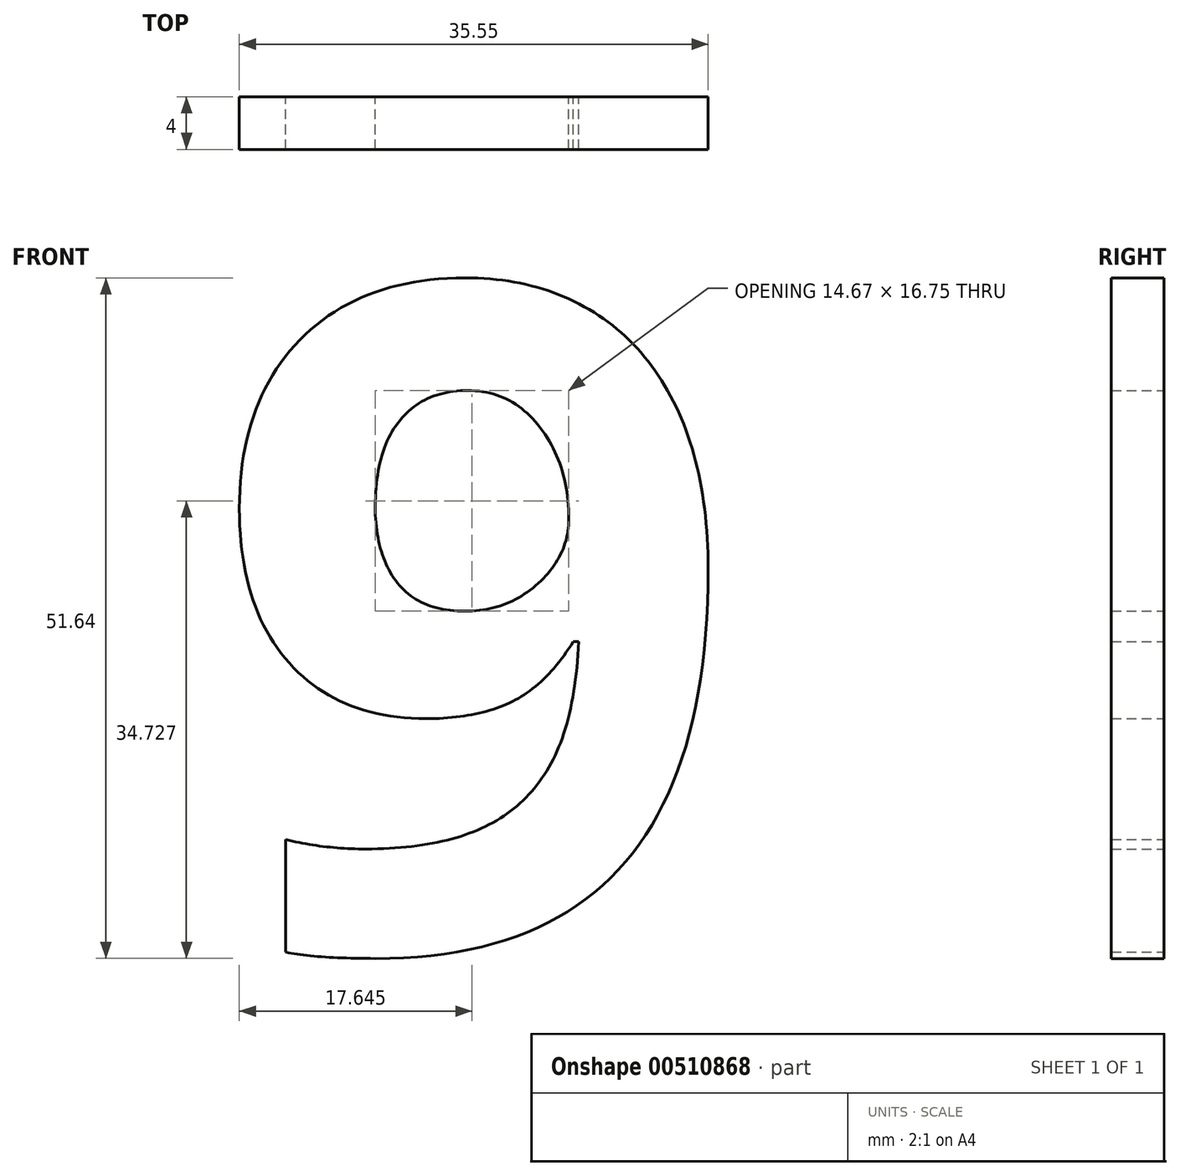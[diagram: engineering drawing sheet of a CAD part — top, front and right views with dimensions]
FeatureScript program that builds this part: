
annotation { "Feature Type Name" : "Feature", "Feature Type Description" : "" }
export const myFeature = defineFeature(function(context is Context, id is Id, definition is map)
    precondition{}
    {
        {
            var Q0;
            Q0=qCreatedBy(makeId("Front.planeOp"),FACE);
            var sketch = newSketch(context, id + "F0", { "sketchPlane" : qUnion([Q0])});
            skText(sketch, "E0", { "text": "9", "fontName": "OpenSans-Bold.ttf"});
            const initialGuessF0  = {"E0": [0, 0, 1, 0, 0.0508]};
            skSetInitialGuess(sketch, initialGuessF0);
            skSolve(sketch);
        }
        {
            var Q0;
            Q0=makeQuery(id+"F0.imprint","IMPRINT",FACE,{"disambiguationData":[TD([[makeQuery(id+"F0.imprint","IMPRINT",EDGE,{"derivedFrom":sQuery(id+"F0.wireOp",EDGE,"E0.sketch_text.stroke-0")}),-1.0]])]});
            extrude(context, id + "F1", {"entities" : qUnion([Q0]), "depth" : 4 * mm});
        }
    });
